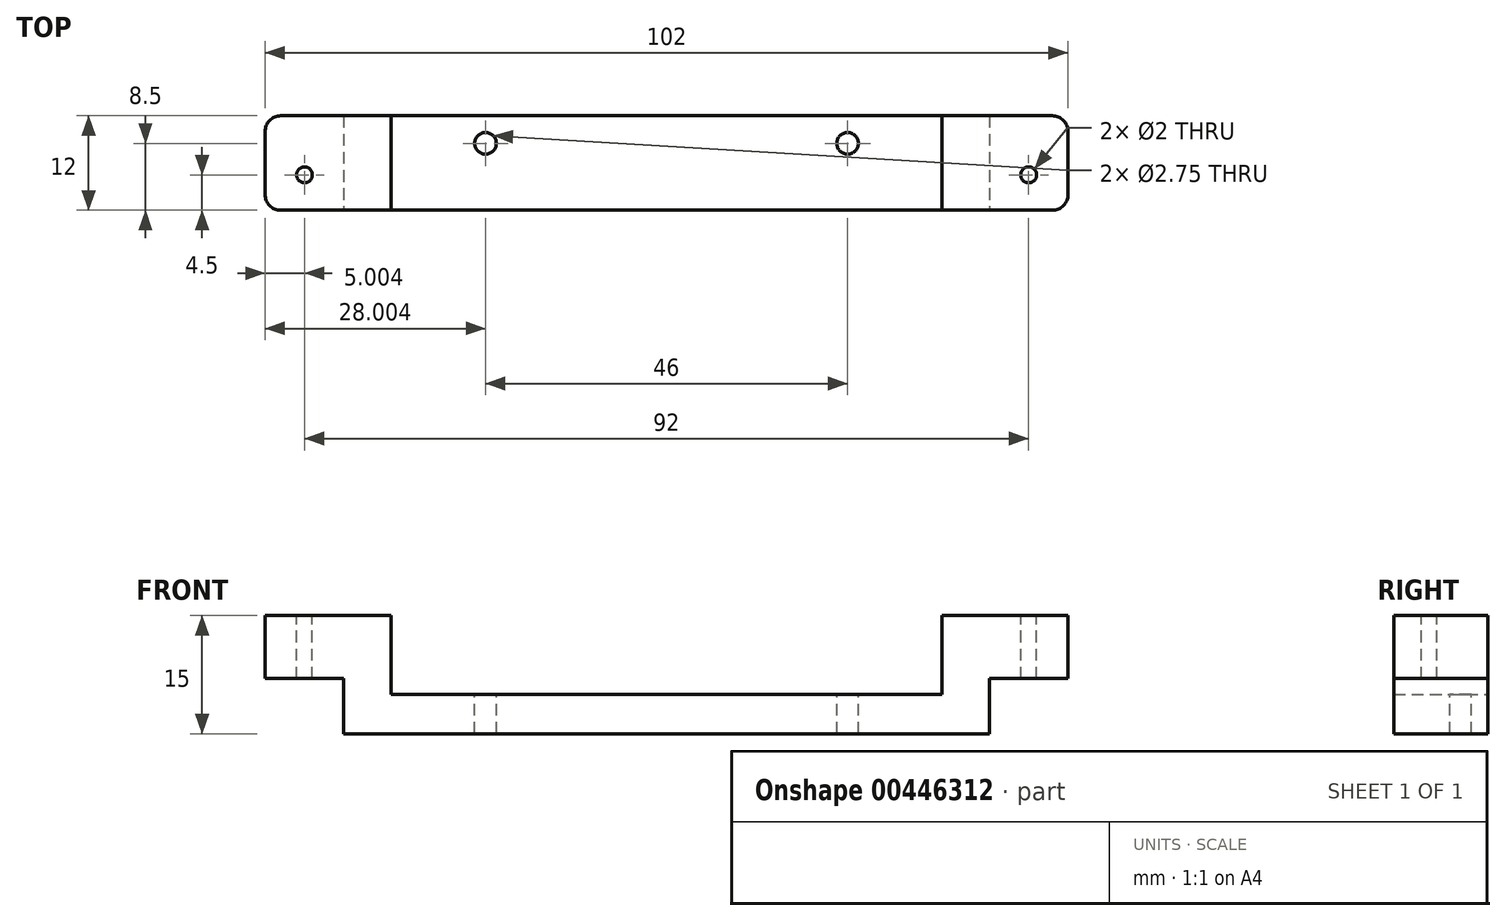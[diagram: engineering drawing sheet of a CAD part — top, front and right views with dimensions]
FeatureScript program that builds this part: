
annotation { "Feature Type Name" : "Feature", "Feature Type Description" : "" }
export const myFeature = defineFeature(function(context is Context, id is Id, definition is map)
    precondition{}
    {
        {
            var Q0;
            Q0=qCreatedBy(makeId("Top.planeOp"),FACE);
            var sketch = newSketch(context, id + "F0", { "sketchPlane" : qUnion([Q0])});
            skLineSegment(sketch, "E0.bottom", {"start": v(-13.49, 0) * mm, "end": v(84.51, 0) * mm});
            skLineSegment(sketch, "E0.top", {"start": v(-13.49, 12) * mm, "end": v(84.51, 12) * mm});
            skLineSegment(sketch, "E0.left", {"start": v(-15.49, 2) * mm, "end": v(-15.49, 10) * mm});
            skLineSegment(sketch, "E0.right", {"start": v(86.51, 2) * mm, "end": v(86.51, 10) * mm});
            skPoint(sketch, "E1.visualSharp", {"position": v(-15.49, 12) * mm});
            skArc(sketch, "E1.filletArc", {"start": v(-13.49, 12) * mm, "mid": v(-14.9, 11.41) * mm, "end": v(-15.49, 10) * mm});
            skPoint(sketch, "E2.visualSharp", {"position": v(-15.49, 0) * mm});
            skArc(sketch, "E2.filletArc", {"start": v(-15.49, 2) * mm, "mid": v(-14.9, 0.59) * mm, "end": v(-13.49, 0) * mm});
            skPoint(sketch, "E3.visualSharp", {"position": v(86.51, 12) * mm});
            skArc(sketch, "E3.filletArc", {"start": v(86.51, 10) * mm, "mid": v(85.93, 11.41) * mm, "end": v(84.51, 12) * mm});
            skPoint(sketch, "E4.visualSharp", {"position": v(86.51, 0) * mm});
            skArc(sketch, "E4.filletArc", {"start": v(84.51, 0) * mm, "mid": v(85.93, 0.59) * mm, "end": v(86.51, 2) * mm});
            skSolve(sketch);
        }
        {
            var Q0;
            Q0=qSketchRegion(id+"F0",true);
            extrude(context, id + "F1", {"entities" : qUnion([Q0]), "depth" : 15 * mm});
        }
        {
            var Q0;
            Q0=makeQuery(id+"F1.opExtrude","CAP_FACE",FACE,{"disambiguationData":[OSD([sQuery(id+"F0.wireOp",EDGE,"E0.bottom"),sQuery(id+"F0.wireOp",EDGE,"E0.top"),sQuery(id+"F0.wireOp",EDGE,"E0.left"),sQuery(id+"F0.wireOp",EDGE,"E0.right"),sQuery(id+"F0.wireOp",EDGE,"E1.filletArc"),sQuery(id+"F0.wireOp",EDGE,"E2.filletArc"),sQuery(id+"F0.wireOp",EDGE,"E3.filletArc"),sQuery(id+"F0.wireOp",EDGE,"E4.filletArc")])],"isStart":false});
            var sketch = newSketch(context, id + "F2", { "sketchPlane" : qUnion([Q0])});
            skLineSegment(sketch, "E5.bottom", {"start": v(0.51, 0) * mm, "end": v(70.51, 0) * mm});
            skLineSegment(sketch, "E5.top", {"start": v(0.51, 12) * mm, "end": v(70.51, 12) * mm});
            skLineSegment(sketch, "E5.left", {"start": v(0.51, 0) * mm, "end": v(0.51, 12) * mm});
            skLineSegment(sketch, "E5.right", {"start": v(70.51, 0) * mm, "end": v(70.51, 12) * mm});
            skPoint(sketch, "E6.visualSharp", {"position": v(0.51, 12) * mm});
            skLineSegment(sketch, "E6.filletArc", {"start": v(0.51, 12) * mm, "end": v(0.51, 12) * mm});
            skPoint(sketch, "E7.visualSharp", {"position": v(0.51, 0) * mm});
            skLineSegment(sketch, "E7.filletArc", {"start": v(0.51, 0) * mm, "end": v(0.51, 0) * mm});
            skPoint(sketch, "E8.visualSharp", {"position": v(70.51, 0) * mm});
            skLineSegment(sketch, "E8.filletArc", {"start": v(70.51, 0) * mm, "end": v(70.51, 0) * mm});
            skPoint(sketch, "E9.visualSharp", {"position": v(70.51, 12) * mm});
            skLineSegment(sketch, "E9.filletArc", {"start": v(70.51, 12) * mm, "end": v(70.51, 12) * mm});
            skSolve(sketch);
        }
        {
            var Q0;
            Q0=qSketchRegion(id+"F2",true);
            extrude(context, id + "F3", {"entities" : qUnion([Q0]), "operationType" : NewBodyOperationType.REMOVE, "oppositeDirection" : true, "depth" : 10 * mm});
        }
        {
            var Q0;
            Q0=makeQuery(id+"F3.boolean.opBoolean","COPY",FACE,{"derivedFrom":makeQuery(id+"F3.opExtrude","CAP_FACE",FACE,{"disambiguationData":[OSD([sQuery(id+"F2.wireOp",EDGE,"E5.bottom"),sQuery(id+"F2.wireOp",EDGE,"E5.top"),sQuery(id+"F2.wireOp",EDGE,"E5.left"),sQuery(id+"F2.wireOp",EDGE,"E5.right")])],"isStart":false})});
            var sketch = newSketch(context, id + "F4", { "sketchPlane" : qUnion([Q0])});
            skCircle(sketch, "E10", {"center": v(12.51, 8.5) * mm, "radius": 1.38 * mm});
            skCircle(sketch, "E11", {"center": v(58.51, 8.5) * mm, "radius": 1.38 * mm});
            skCircle(sketch, "E12", {"center": v(-10.49, 4.5) * mm, "radius": 1 * mm});
            skCircle(sketch, "E13", {"center": v(81.51, 4.5) * mm, "radius": 1 * mm});
            skSolve(sketch);
        }
        {
            var Q0;
            Q0=qSketchRegion(id+"F4",true);
            extrude(context, id + "F5", {"entities" : qUnion([Q0]), "operationType" : NewBodyOperationType.REMOVE, "oppositeDirection" : true, "depth" : 25 * mm, "hasSecondDirection" : true, "secondDirectionOppositeDirection" : false, "secondDirectionDepth" : 25 * mm});
        }
        {
            var Q0;
            Q0=makeQuery(id+"F1.opExtrude","CAP_FACE",FACE,{"disambiguationData":[OSD([sQuery(id+"F0.wireOp",EDGE,"E0.bottom"),sQuery(id+"F0.wireOp",EDGE,"E0.top"),sQuery(id+"F0.wireOp",EDGE,"E0.left"),sQuery(id+"F0.wireOp",EDGE,"E0.right"),sQuery(id+"F0.wireOp",EDGE,"E1.filletArc"),sQuery(id+"F0.wireOp",EDGE,"E2.filletArc"),sQuery(id+"F0.wireOp",EDGE,"E3.filletArc"),sQuery(id+"F0.wireOp",EDGE,"E4.filletArc")])],"isStart":true});
            var sketch = newSketch(context, id + "F6", { "sketchPlane" : qUnion([Q0])});
            skLineSegment(sketch, "E14.bottom", {"start": v(-5.49, -12) * mm, "end": v(-15.58, -12) * mm});
            skLineSegment(sketch, "E14.top", {"start": v(-5.49, 0) * mm, "end": v(-15.58, 0) * mm});
            skLineSegment(sketch, "E14.left", {"start": v(-5.49, -12) * mm, "end": v(-5.49, 0) * mm});
            skLineSegment(sketch, "E14.right", {"start": v(-15.58, -12) * mm, "end": v(-15.58, 0) * mm});
            skLineSegment(sketch, "E15.bottom", {"start": v(76.51, -12) * mm, "end": v(86.64, -12) * mm});
            skLineSegment(sketch, "E15.top", {"start": v(76.51, 0) * mm, "end": v(86.64, 0) * mm});
            skLineSegment(sketch, "E15.left", {"start": v(76.51, -12) * mm, "end": v(76.51, 0) * mm});
            skLineSegment(sketch, "E15.right", {"start": v(86.64, -12) * mm, "end": v(86.64, 0) * mm});
            skSolve(sketch);
        }
        {
            var Q0;
            {var subQ1=sQuery(id+"F6.wireOp",EDGE,"E15.left");Q0=makeQuery(id+"F6.imprint","IMPRINT",FACE,{"disambiguationData":[TD([[makeQuery(id+"F6.imprint","IMPRINT",EDGE,{"derivedFrom":subQ1}),-1.0]])]});}
            var Q1;
            {var subQ1=sQuery(id+"F6.wireOp",EDGE,"E14.left");Q1=makeQuery(id+"F6.imprint","IMPRINT",FACE,{"disambiguationData":[TD([[makeQuery(id+"F6.imprint","IMPRINT",EDGE,{"derivedFrom":subQ1}),1.0]])]});}
            extrude(context, id + "F7", {"entities" : qUnion([Q0, Q1]), "operationType" : NewBodyOperationType.REMOVE, "oppositeDirection" : true, "depth" : 7 * mm});
        }
    });
